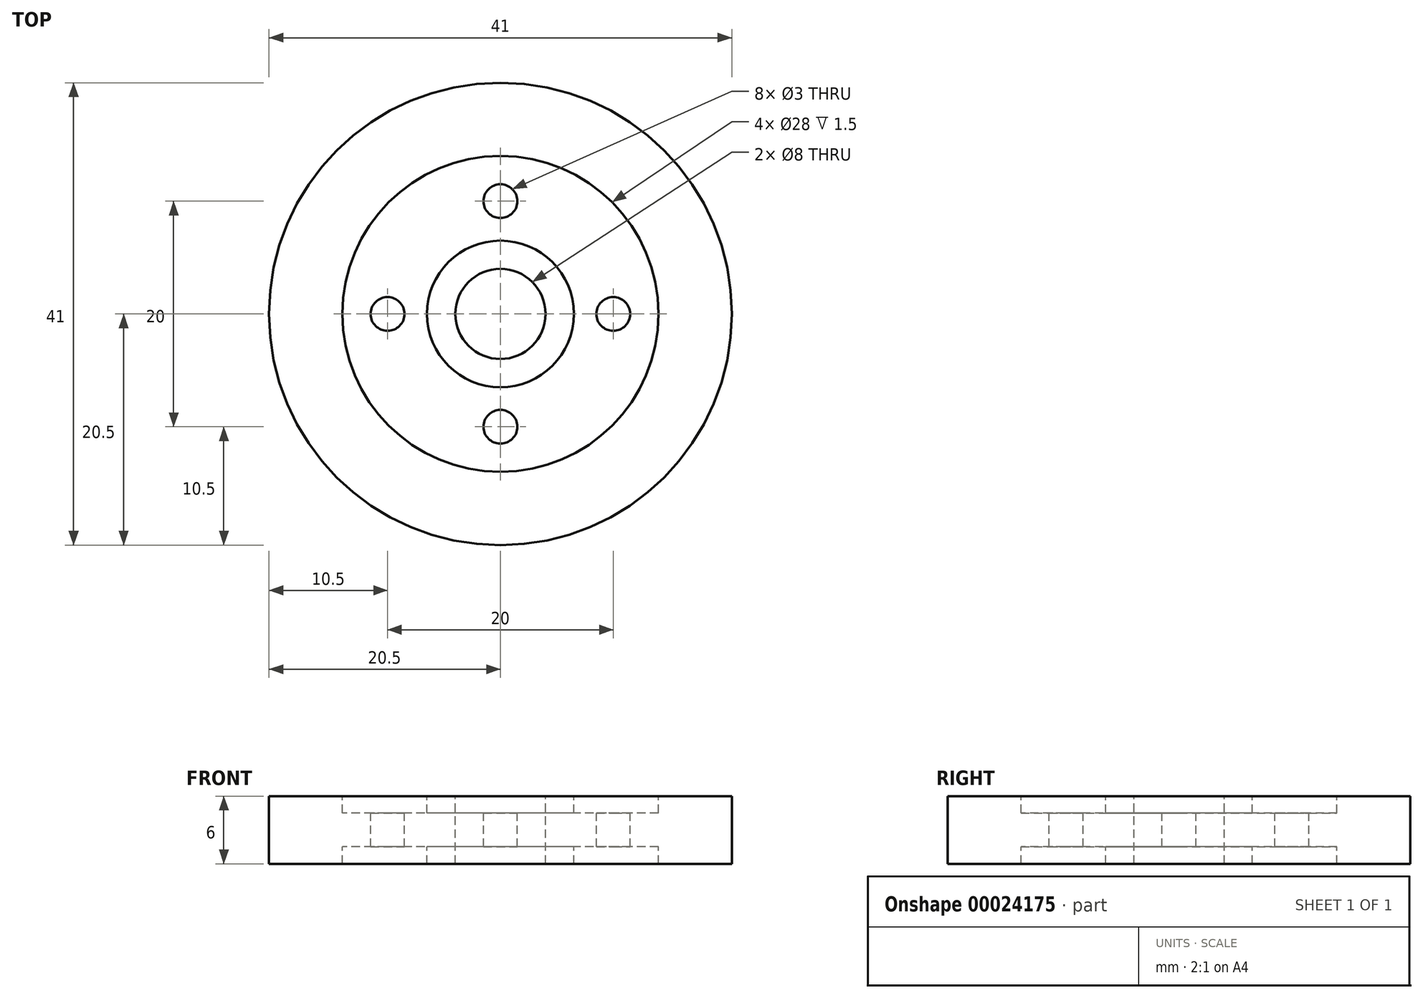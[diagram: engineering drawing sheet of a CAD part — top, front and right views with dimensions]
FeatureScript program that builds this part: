
annotation { "Feature Type Name" : "Feature", "Feature Type Description" : "" }
export const myFeature = defineFeature(function(context is Context, id is Id, definition is map)
    precondition{}
    {
        {
            var Q0;
            Q0=qCreatedBy(makeId("Front.planeOp"),FACE);
            var sketch = newSketch(context, id + "F0", { "sketchPlane" : qUnion([Q0])});
            skLineSegment(sketch, "E0", {"start": v(0, 27.45) * mm, "end": v(0, -30.73) * mm, "construction": true});
            skLineSegment(sketch, "E1.bottom", {"start": v(4, 8) * mm, "end": v(6.5, 8) * mm});
            skLineSegment(sketch, "E1.top", {"start": v(4, 2) * mm, "end": v(6.5, 2) * mm});
            skLineSegment(sketch, "E1.left", {"start": v(4, 8) * mm, "end": v(4, 2) * mm});
            skLineSegment(sketch, "E1.right", {"start": v(6.5, 8) * mm, "end": v(6.5, 2) * mm});
            skLineSegment(sketch, "E2.bottom", {"start": v(6.5, 6.5) * mm, "end": v(14, 6.5) * mm});
            skLineSegment(sketch, "E2.top", {"start": v(6.5, 3.5) * mm, "end": v(14, 3.5) * mm});
            skLineSegment(sketch, "E2.left", {"start": v(6.5, 6.5) * mm, "end": v(6.5, 3.5) * mm});
            skLineSegment(sketch, "E2.right", {"start": v(14, 6.5) * mm, "end": v(14, 3.5) * mm});
            skLineSegment(sketch, "E3.bottom", {"start": v(14, 8) * mm, "end": v(20.5, 8) * mm});
            skLineSegment(sketch, "E3.top", {"start": v(14, 2) * mm, "end": v(20.5, 2) * mm});
            skLineSegment(sketch, "E3.left", {"start": v(14, 8) * mm, "end": v(14, 2) * mm});
            skLineSegment(sketch, "E3.right", {"start": v(20.5, 8) * mm, "end": v(20.5, 2) * mm});
            skSolve(sketch);
        }
        {
            var Q0;
            {var subQ3=sQuery(id+"F0.wireOp",EDGE,"E1.bottom");Q0=makeQuery(id+"F0.imprint","IMPRINT",FACE,{"disambiguationData":[TD([[makeQuery(id+"F0.imprint","IMPRINT",EDGE,{"derivedFrom":subQ3}),-1.0]])]});}
            var Q1;
            {var subQ2=sQuery(id+"F0.wireOp",EDGE,"E2.bottom");Q1=makeQuery(id+"F0.imprint","IMPRINT",FACE,{"disambiguationData":[TD([[makeQuery(id+"F0.imprint","IMPRINT",EDGE,{"derivedFrom":subQ2}),-1.0]])]});}
            var Q2;
            {var subQ4=sQuery(id+"F0.wireOp",EDGE,"E3.bottom");Q2=makeQuery(id+"F0.imprint","IMPRINT",FACE,{"disambiguationData":[TD([[makeQuery(id+"F0.imprint","IMPRINT",EDGE,{"derivedFrom":subQ4}),-1.0]])]});}
            var Q3;
            Q3=sQuery(id+"F0.wireOp",EDGE,"E0");
            revolve(context, id + "F1", {"entities" : qUnion([Q0, Q1, Q2]), "axis" : qUnion([Q3]), "revolveType" : RevolveType.FULL});
        }
        {
            var Q0;
            Q0=makeQuery(id+"F1.opRevolve","SWEPT_FACE",FACE,{"disambiguationData":[OSD([sQuery(id+"F0.wireOp",EDGE,"E2.bottom")])]});
            var sketch = newSketch(context, id + "F2", { "sketchPlane" : qUnion([Q0])});
            skCircle(sketch, "E4", {"center": v(0, 10) * mm, "radius": 1.5 * mm});
            skPoint(sketch, "E5", {"position": v(0, 0) * mm});
            skCircle(sketch, "E6", {"center": v(0, 0) * mm, "radius": 7.77 * mm});
            skSolve(sketch);
        }
        {
            var Q0;
            Q0=makeQuery(id+"F2.imprint","IMPRINT",FACE,{"disambiguationData":[TD([[makeQuery(id+"F2.imprint","IMPRINT",EDGE,{"derivedFrom":sQuery(id+"F2.wireOp",EDGE,"E4")}),1.0]])]});
            extrude(context, id + "F3", {"entities" : qUnion([Q0]), "operationType" : NewBodyOperationType.REMOVE, "oppositeDirection" : true, "depth" : 25.4 * mm});
        }
        {
            var Q0;
            Q0=makeQuery(id+"F1.opRevolve","SWEPT_BODY",BODY,{"disambiguationData":[OSD([sQuery(id+"F0.wireOp",EDGE,"E1.bottom"),sQuery(id+"F0.wireOp",EDGE,"E1.top"),sQuery(id+"F0.wireOp",EDGE,"E1.left"),sQuery(id+"F0.wireOp",EDGE,"E1.right"),sQuery(id+"F0.wireOp",EDGE,"E2.bottom"),sQuery(id+"F0.wireOp",EDGE,"E2.top"),sQuery(id+"F0.wireOp",EDGE,"E3.bottom"),sQuery(id+"F0.wireOp",EDGE,"E3.top"),sQuery(id+"F0.wireOp",EDGE,"E3.left"),sQuery(id+"F0.wireOp",EDGE,"E3.right")])]});
            var Q1;
            Q1=makeQuery(id+"F3.boolean.opBoolean","COPY",FACE,{"derivedFrom":makeQuery(id+"F3.opExtrude","SWEPT_FACE",FACE,{"disambiguationData":[OSD([sQuery(id+"F2.wireOp",EDGE,"E4")])]})});
            var Q2;
            Q2=makeQuery(id+"F1.opRevolve","SWEPT_FACE",FACE,{"disambiguationData":[OSD([sQuery(id+"F0.wireOp",EDGE,"E1.left")])]});
            circularPattern(context, id + "F4", {"faces" : qUnion([Q1]), "axis" : qUnion([Q2]), "angle" : 360 * degree, "instanceCount" : 4, "equalSpace" : true, "patternType" : PatternType.FACE});
        }
        {
            var Q0;
            Q0=makeQuery(id+"F1.opRevolve","SWEPT_BODY",BODY,{"disambiguationData":[OSD([sQuery(id+"F0.wireOp",EDGE,"E1.bottom"),sQuery(id+"F0.wireOp",EDGE,"E1.top"),sQuery(id+"F0.wireOp",EDGE,"E1.left"),sQuery(id+"F0.wireOp",EDGE,"E1.right"),sQuery(id+"F0.wireOp",EDGE,"E2.bottom"),sQuery(id+"F0.wireOp",EDGE,"E2.top"),sQuery(id+"F0.wireOp",EDGE,"E3.bottom"),sQuery(id+"F0.wireOp",EDGE,"E3.top"),sQuery(id+"F0.wireOp",EDGE,"E3.left"),sQuery(id+"F0.wireOp",EDGE,"E3.right")])]});
            transform(context, id + "F5", {"entities" : qUnion([Q0]), "transformType" : TransformType.TRANSLATION_3D, "dx" : 0 * mm, "dy" : 0 * mm, "dz" : 0 * mm, "makeCopy" : true});
        }
    });
